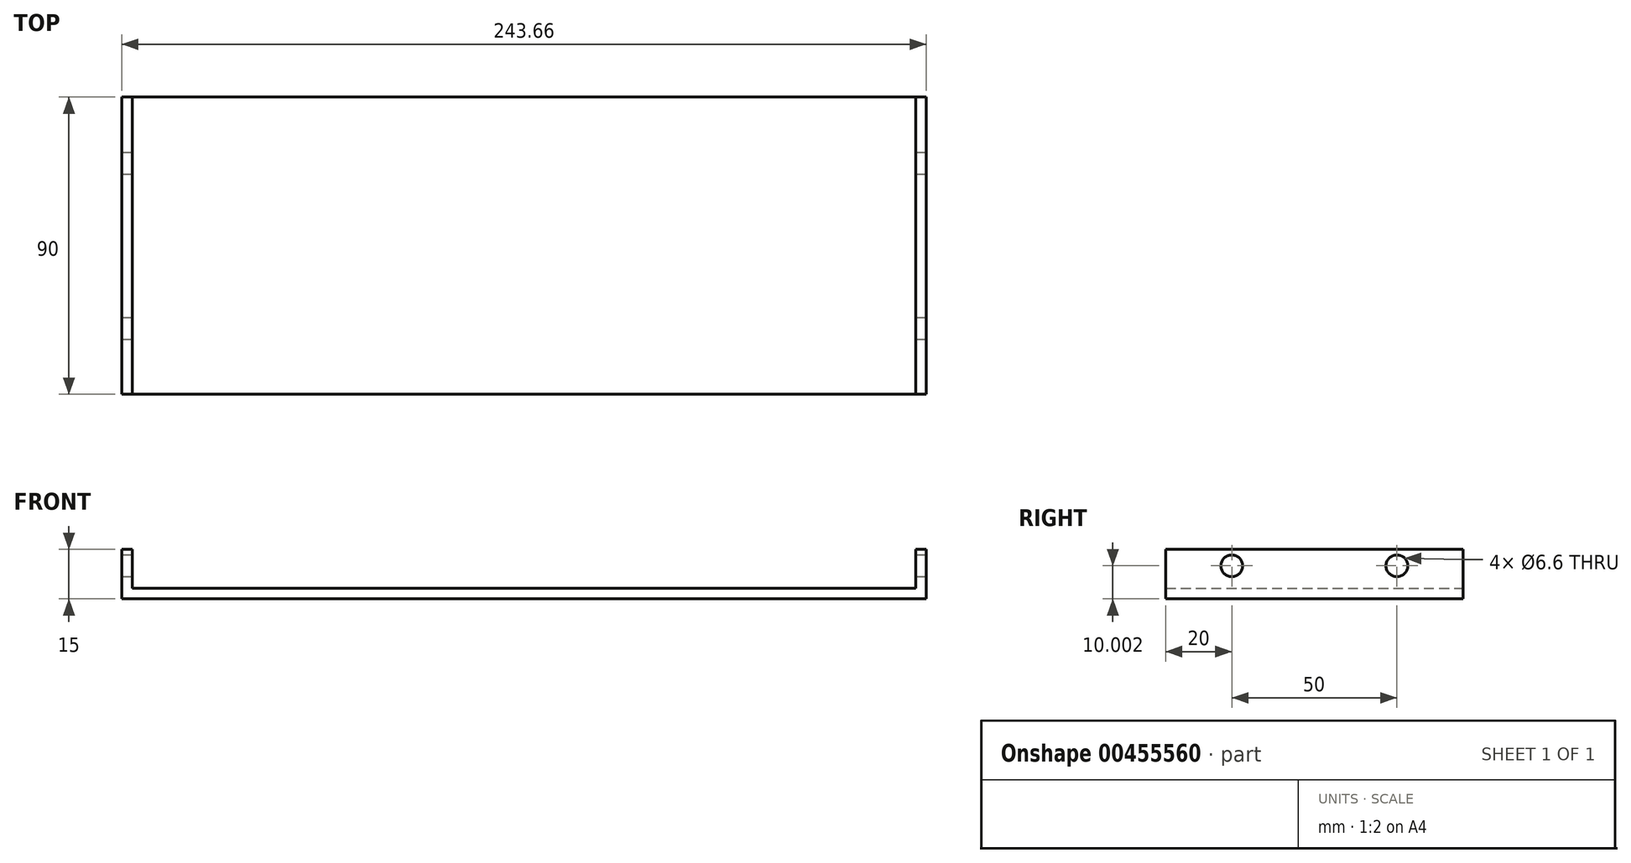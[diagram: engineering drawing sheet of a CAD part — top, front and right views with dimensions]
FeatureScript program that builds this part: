
annotation { "Feature Type Name" : "Feature", "Feature Type Description" : "" }
export const myFeature = defineFeature(function(context is Context, id is Id, definition is map)
    precondition{}
    {
        {
            var Q0;
            Q0=qCreatedBy(makeId("Front.planeOp"),FACE);
            var sketch = newSketch(context, id + "F0", { "sketchPlane" : qUnion([Q0])});
            skLineSegment(sketch, "E0.bottom", {"start": v(118.65, 1.59) * mm, "end": v(-118.65, 1.59) * mm});
            skLineSegment(sketch, "E0.top", {"start": v(121.83, -1.59) * mm, "end": v(-121.83, -1.59) * mm});
            skLineSegment(sketch, "E0.left", {"start": v(121.83, 1.59) * mm, "end": v(121.83, -1.59) * mm});
            skLineSegment(sketch, "E0.right", {"start": v(-121.83, 1.59) * mm, "end": v(-121.83, -1.59) * mm});
            skPoint(sketch, "E0.middle", {"position": v(0, 0) * mm});
            skLineSegment(sketch, "E1.bottom", {"start": v(-121.83, -1.59) * mm, "end": v(-118.65, -1.59) * mm});
            skLineSegment(sketch, "E1.top", {"start": v(-121.83, 13.41) * mm, "end": v(-118.65, 13.41) * mm});
            skLineSegment(sketch, "E1.left", {"start": v(-121.83, -1.59) * mm, "end": v(-121.83, 13.41) * mm});
            skLineSegment(sketch, "E1.right", {"start": v(-118.65, 1.59) * mm, "end": v(-118.65, 13.41) * mm});
            skLineSegment(sketch, "E2.MirrorCS", {"start": v(118.65, 1.59) * mm, "end": v(118.65, 13.41) * mm});
            skLineSegment(sketch, "E3.MirrorCS", {"start": v(121.83, -1.59) * mm, "end": v(121.83, 13.41) * mm});
            skLineSegment(sketch, "E4.MirrorCS", {"start": v(121.83, -1.59) * mm, "end": v(118.65, -1.59) * mm});
            skLineSegment(sketch, "E5.MirrorCS", {"start": v(121.83, 13.41) * mm, "end": v(118.65, 13.41) * mm});
            skSolve(sketch);
        }
        {
            var Q0;
            Q0=makeQuery(id+"F0.imprint","IMPRINT",FACE,{"disambiguationData":[TD([[makeQuery(id+"F0.imprint","IMPRINT",EDGE,{"derivedFrom":sQuery(id+"F0.wireOp",EDGE,"E0.bottom")}),1.0]])]});
            extrude(context, id + "F1", {"entities" : qUnion([Q0]), "endBound" : BoundingType.SYMMETRIC, "depth" : 90 * mm});
        }
        {
            var Q0;
            Q0=makeQuery(id+"F1.opExtrude","SWEPT_FACE",FACE,{"disambiguationData":[OSD([sQuery(id+"F0.wireOp",EDGE,"E3.MirrorCS")])]});
            var sketch = newSketch(context, id + "F2", { "sketchPlane" : qUnion([Q0])});
            skCircle(sketch, "E6", {"center": v(-25, 8.41) * mm, "radius": 3.3 * mm});
            skCircle(sketch, "E7.MirrorC", {"center": v(25, 8.41) * mm, "radius": 3.3 * mm});
            skSolve(sketch);
        }
        {
            var Q0;
            Q0 = qSketchRegion(id + "F2", true);
            extrude(context, id + "F3", {"entities" : qUnion([Q0]), "operationType" : NewBodyOperationType.REMOVE, "endBound" : BoundingType.THROUGH_ALL, "oppositeDirection" : true, "depth" : 25 * mm});
        }
    });
